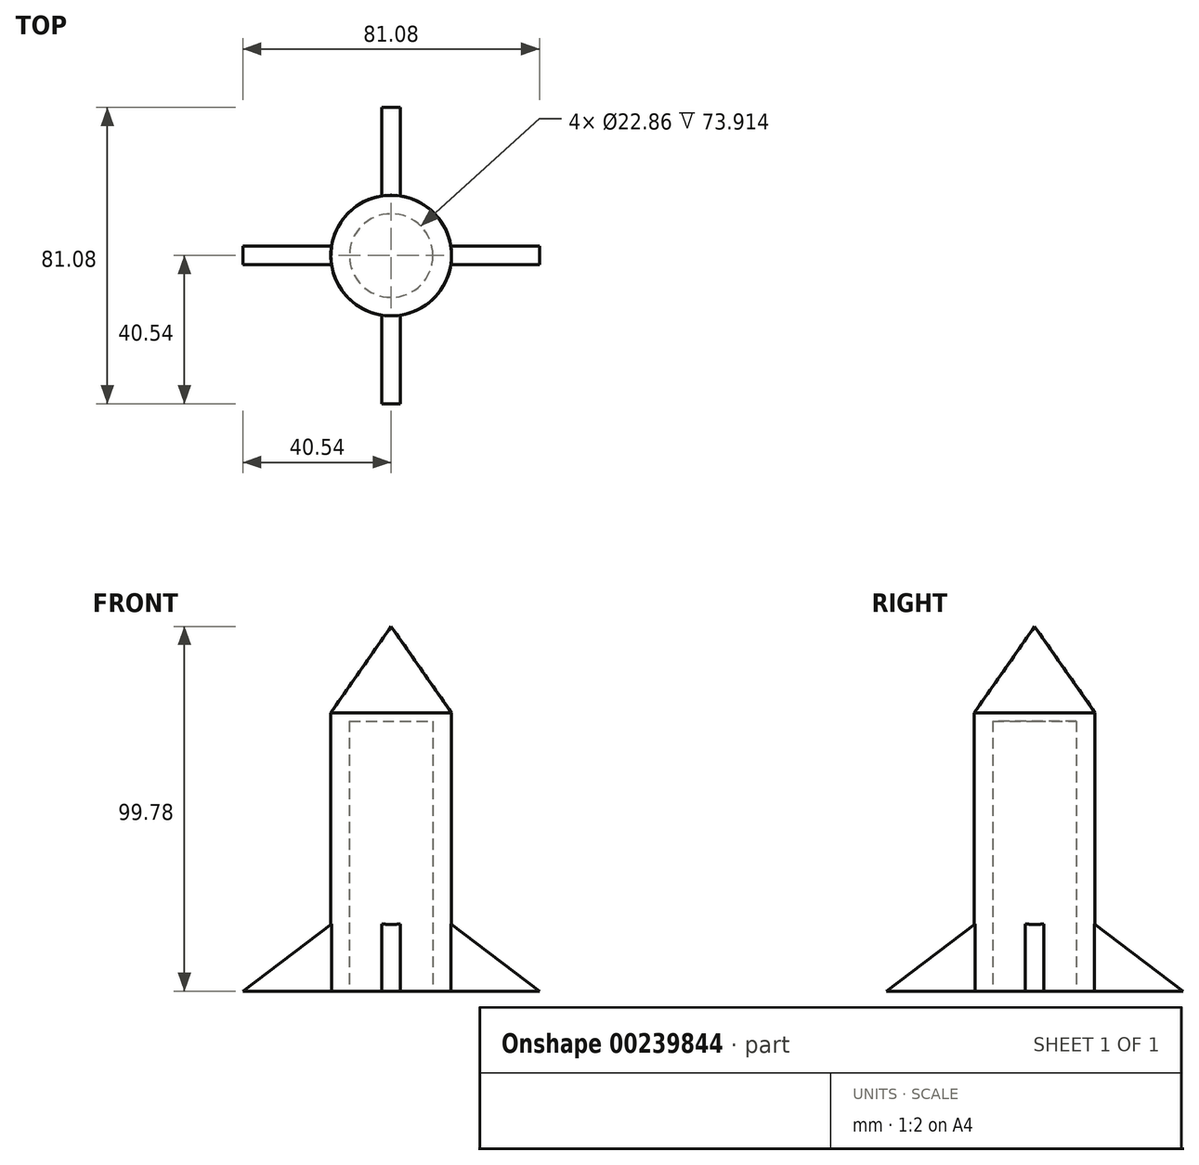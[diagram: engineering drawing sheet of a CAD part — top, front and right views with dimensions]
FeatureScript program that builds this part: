
annotation { "Feature Type Name" : "Feature", "Feature Type Description" : "" }
export const myFeature = defineFeature(function(context is Context, id is Id, definition is map)
    precondition{}
    {
        {
            var Q0;
            Q0=qCreatedBy(makeId("Top.planeOp"),FACE);
            var sketch = newSketch(context, id + "F0", { "sketchPlane" : qUnion([Q0])});
            skCircle(sketch, "E0", {"center": v(0, 0) * mm, "radius": 16.51 * mm});
            skCircle(sketch, "E1", {"center": v(0, 0) * mm, "radius": 12.7 * mm});
            skSolve(sketch);
        }
        {
            var Q0;
            Q0=makeQuery(id+"F0.imprint","IMPRINT",FACE,{"disambiguationData":[TD([[makeQuery(id+"F0.imprint","IMPRINT",EDGE,{"derivedFrom":sQuery(id+"F0.wireOp",EDGE,"E0")}),1.0]])]});
            var Q1;
            Q1=makeQuery(id+"F0.imprint","IMPRINT",FACE,{"disambiguationData":[TD([[makeQuery(id+"F0.imprint","IMPRINT",EDGE,{"derivedFrom":sQuery(id+"F0.wireOp",EDGE,"E1")}),1.0]])]});
            extrude(context, id + "F1", {"entities" : qUnion([Q0, Q1]), "depth" : 76.2 * mm});
        }
        {
            var Q0;
            Q0=makeQuery(id+"F1.opExtrude","CAP_FACE",FACE,{"disambiguationData":[OSD([sQuery(id+"F0.wireOp",EDGE,"E0")])],"isStart":false});
            extrude(context, id + "F2", {"entities" : qUnion([Q0]), "operationType" : NewBodyOperationType.ADD, "depth" : 25.4 * mm, "hasDraft" : true, "draftAngle" : 35 * degree, "draftPullDirection" : true});
        }
        {
            var Q0;
            Q0=qCreatedBy(makeId("Right.planeOp"),FACE);
            var sketch = newSketch(context, id + "F3", { "sketchPlane" : qUnion([Q0])});
            skLineSegment(sketch, "E2", {"start": v(-15.85, 0) * mm, "end": v(-15.85, 18.75) * mm});
            skLineSegment(sketch, "E3", {"start": v(-15.85, 18.75) * mm, "end": v(-40.54, 0) * mm});
            skLineSegment(sketch, "E4", {"start": v(-40.54, 0) * mm, "end": v(-15.85, 0) * mm});
            skSolve(sketch);
        }
        {
            var Q0;
            Q0 = qSketchRegion(id + "F3", true);
            extrude(context, id + "F4", {"entities" : qUnion([Q0]), "operationType" : NewBodyOperationType.ADD, "endBound" : BoundingType.SYMMETRIC, "depth" : 5.08 * mm});
        }
        {
            var Q0;
            Q0=makeQuery(id+"F1.opExtrude","SWEPT_BODY",BODY,{"disambiguationData":[OSD([sQuery(id+"F0.wireOp",EDGE,"E0")])]});
            var Q1;
            {var subQ0=sQuery(id+"F0.wireOp",EDGE,"E0");Q1=makeQuery(id+"F2.boolean.opBoolean","MERGE",EDGE,{"derivedFrom":[makeQuery(id+"F1.opExtrude","CAP_EDGE",EDGE,{"disambiguationData":[OSD([subQ0])],"isStart":false}),makeQuery(id+"F2.opExtrude","CAP_EDGE",EDGE,{"disambiguationData":[OSD([subQ0])],"isStart":true})]});}
            circularPattern(context, id + "F5", {"entities" : qUnion([Q0]), "axis" : qUnion([Q1]), "angle" : 360 * degree, "instanceCount" : 4, "equalSpace" : true});
        }
        {
            var Q0;
            Q0=makeQuery(id+"F4.boolean.opBoolean","MERGE",FACE,{"derivedFrom":[makeQuery(id+"F1.opExtrude","CAP_FACE",FACE,{"disambiguationData":[OSD([sQuery(id+"F0.wireOp",EDGE,"E0")])],"isStart":true}),makeQuery(id+"F4.opExtrude","SWEPT_FACE",FACE,{"disambiguationData":[OSD([sQuery(id+"F3.wireOp",EDGE,"E4")])]})]});
            var sketch = newSketch(context, id + "F6", { "sketchPlane" : qUnion([Q0])});
            skCircle(sketch, "E5", {"center": v(0, 0) * mm, "radius": 11.43 * mm});
            skSolve(sketch);
        }
        {
            var Q0;
            Q0 = qSketchRegion(id + "F6", true);
            extrude(context, id + "F7", {"entities" : qUnion([Q0]), "operationType" : NewBodyOperationType.REMOVE, "oppositeDirection" : true, "depth" : 73.9 * mm});
        }
    });
